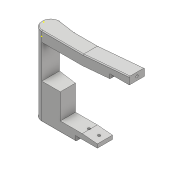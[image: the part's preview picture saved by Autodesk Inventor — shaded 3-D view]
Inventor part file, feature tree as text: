
AUTODESK INVENTOR PART (.ipt)
format: ipt  version: 2017 (Build 210142000, 142)  size: 240,128 bytes
history: native  units: mm
features: sketch x14, extrude x12, plane x2, fillet x1
ambient origin geometry x8: Origin, YZ Plane, XZ Plane, XY Plane, X Axis, Y Axis, Z Axis, Center Point
bodies: Solid1 (feature_tree)
feature tree (29):
  extrude  "Extrusion1"  Depth=18.0mm
  extrude  "Extrusion2"  Depth=10.5mm
  extrude  "Extrusion3"  Depth=102.0mm TaperAngle=0.0deg
  plane  "Work Plane1"
  extrude  "Extrusion4"  Depth=59.5mm
  extrude  "Extrusion5"  Depth=102.0mm TaperAngle=0.0deg
  plane  "Work Plane2"
  extrude  "Extrusion6"  Depth=6.0mm
  extrude  "Extrusion7"  Depth=36.0mm
  fillet  "Fillet1"  Radius=15.0mm
  extrude  "Extrusion8"  Depth=22.0mm
  extrude  "Extrusion9"  Depth=22.0mm
  extrude  "Extrusion10"  Depth=30.0mm
  extrude  "Extrusion11"  Depth=26.0mm
  extrude  "Extrusion12"  Depth=36.0mm
  sketch  "Sketch14"  dims[d27=15.0mm]
  sketch  "Sketch15"  dims[d28=20.071286mm d29=102.0mm d30=0.0mm d31=-6.0mm d32=38.0mm d33=77.0mm d34=0.0mm d35=6.0mm d36=0.0mm d37=-84.0mm d38=23.0mm d39=6.0mm d40=0.0mm d41=3.0mm d42=6.0mm d43=0.0mm d44=1.0mm d45=5.0mm d46=18.0mm d47=6.0mm d48=0.0mm d49=3.0mm d50=3.0mm d51=6.0mm d52=0.0mm d54=3.0mm d55=5.0mm d56=0.0mm d57=3.0mm d58=3.0mm d59=3.0mm d60=3.0mm d61=6.0mm d62=0.0mm d63=22.0mm d64=2.0mm d65=6.0mm d66=0.0mm]
  sketch  "Sketch1"  dims[d0=104.0mm d1=18.0mm]
  sketch  "Sketch2"  dims[d2=21.0mm d3=10.5mm]
  sketch  "Sketch3"  dims[d4=21.0mm d5=102.0mm d6=0.0mm]
  sketch  "Sketch4"  dims[d7=8.0mm d8=59.5mm]
  sketch  "Sketch5"  dims[d9=0.872665mm d10=102.0mm d11=0.0mm]
  sketch  "Sketch6"  dims[d12=6.0mm d13=26.0mm]
  sketch  "Sketch7"  dims[d14=36.0mm d15=30.543262mm d16=15.0mm]
  sketch  "Sketch8"  dims[d17=20.071286mm d18=22.0mm]
  sketch  "Sketch9"  dims[d19=46.0mm d20=22.0mm]
  sketch  "Sketch10"  dims[d21=0.0mm d22=30.0mm]
  sketch  "Sketch11"  dims[d23=90.0deg d24=26.0mm]
  sketch  "Sketch12"  dims[d25=36.0mm d26=30.543262mm]
